# Revit family: 290273 OvaLED R NM ST LED LP 1t_Tak
name_source: partatom
category: Lighting Fixtures
revit_build: Autodesk Revit 2016 (Build: 20160314_0715(x64)
units: mm (PartAtom-declared; Revit-internal decimal feet)

## family parameters
Always vertical = Yes
Cut with Voids When Loaded = No
Light Source = Yes
OmniClass Number = 23.80.70.11.21
OmniClass Title = Emergency Lighting
Part Type = Normal
Room Calculation Point = No
Round Connector Dimension = Use Diameter
Shared = No
Work Plane-Based = No

## types (1)
- Ledelys
    Assembly Code = 4432
    Color Filter = 16777215
    Diameter = 123 mm  [stored 0.403543 ft]
    Dimming Lamp Color Temperature Shift = <None>
    Emit Shape Visible in Rendering = No
    Emit from Rectangle Length = 160 mm  [stored 0.524934 ft]
    Emit from Rectangle Width = 160 mm  [stored 0.524934 ft]
    Glass Material = Plastic - Glass
    Height = 22 mm  [stored 0.0721785 ft]
    Height 1 = 38 mm  [stored 0.124672 ft]
    Height 2 = 35 mm
    Keynote = WT2
    Length A = 160 mm  [stored 0.524934 ft]
    Length B = 160 mm  [stored 0.524934 ft]
    Manufacturer = Honeywell
    Material = Plastic - White
    NS8360 = 4432_WT2
    Number of Poles = 1
    Photometric Web File = 2x4 3Lamp.ies
    Tilt Angle = 90.00°
    Type Comments = -UN
    Voltage = 230 V

note: [stored X ft] marks values corroborated as IEEE doubles in the binary element streams (Revit-internal decimal feet)

## geometry (parser evidence)
native form markers: Blend x2, Sweep x3
no freeform markers — native parametric forms only
